# Revit family: Detention_Desk
name_source: partatom
category: Casework
units: mm (PartAtom-declared; Revit-internal decimal feet)

## family parameters
Always vertical = Yes
Classification Number = 23.40.70.31.17
Cut with Voids When Loaded = No
Room Calculation Point = No
Shared = No
Work Plane-Based = No

## types (1)
- Detention_Desk
    Assembly Code = E1020600
    Construction Details = http://www.arcat.com
    Default Elevation = 0' - 0"
    Depth = 1' - 3"
    Description = Detention Desk
    Desk Material = Metal - Steel, Painted, Orange
    Expected Lifespan (Years) = 10
    Frame Material = Metal - Steel, Painted, Black
    Green Building-LEED = http://www.arcat.com
    Hardware Material = Metal - Brass
    Height = 2' - 6"
    Keynote = 11190
    Maintenance Schedule (Months) = 12
    Manufacturer = Generic
    Manufacturer Fax = (203) 939-2444
    Manufacturer Website = http://www.arcat.com
    Model = Generic
    Product Data = http://www.arcat.com
    Product Properties = http://www.arcat.com
    Seat Height = 1' - 5"
    Specification = http://www.arcat.com
    Stool Material = Metal - Steel, Stainless
    Warranty Duration (Years) = 2
    Width = 2' - 6"

## geometry (parser evidence)
native form markers: Sweep x4
no freeform markers — native parametric forms only
